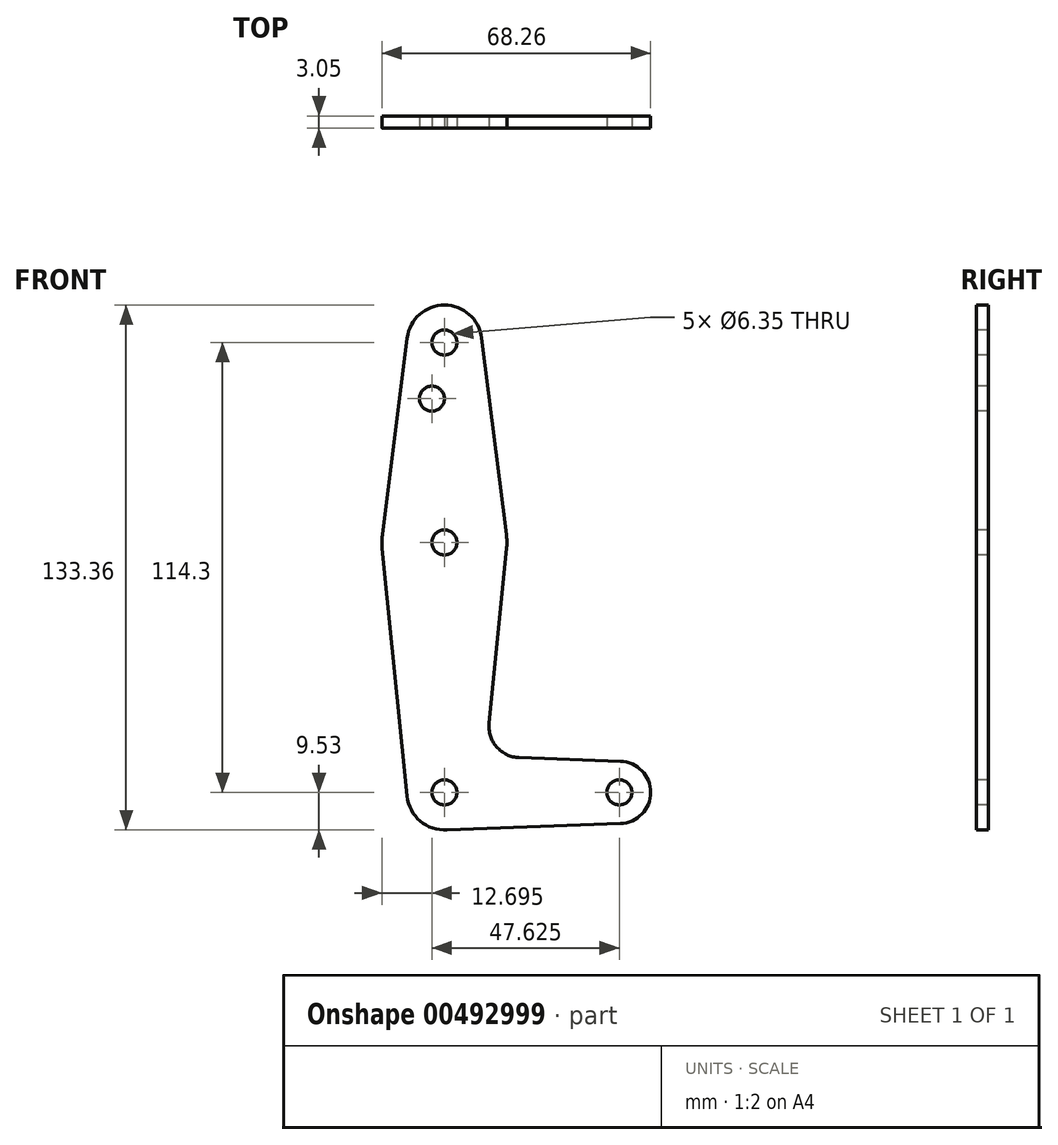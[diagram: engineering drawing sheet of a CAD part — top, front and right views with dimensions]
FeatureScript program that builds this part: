
annotation { "Feature Type Name" : "Feature", "Feature Type Description" : "" }
export const myFeature = defineFeature(function(context is Context, id is Id, definition is map)
    precondition{}
    {
        {
            var Q0;
            Q0=qCreatedBy(makeId("Front.planeOp"),FACE);
            var sketch = newSketch(context, id + "F0", { "sketchPlane" : qUnion([Q0])});
            skCircle(sketch, "E0", {"center": v(0, 0) * mm, "radius": 9.53 * mm});
            skCircle(sketch, "E1", {"center": v(0, 63.5) * mm, "radius": 15.88 * mm});
            skCircle(sketch, "E2", {"center": v(0, 114.3) * mm, "radius": 9.52 * mm});
            skCircle(sketch, "E3", {"center": v(44.45, 0) * mm, "radius": 7.94 * mm});
            skLineSegment(sketch, "E4", {"start": v(0, 0) * mm, "end": v(44.45, 0) * mm, "construction": true});
            skLineSegment(sketch, "E5", {"start": v(0, 114.3) * mm, "end": v(0, 0) * mm, "construction": true});
            skLineSegment(sketch, "E6", {"start": v(-9.45, 115.5) * mm, "end": v(-15.75, 65.48) * mm});
            skLineSegment(sketch, "E7", {"start": v(9.45, 115.5) * mm, "end": v(15.75, 65.48) * mm});
            skLineSegment(sketch, "E8", {"start": v(0, -9.53) * mm, "end": v(44.73, -7.93) * mm});
            skLineSegment(sketch, "E9", {"start": v(18.97, 8.85) * mm, "end": v(44.73, 7.93) * mm});
            skCircle(sketch, "E10", {"center": v(0, 114.3) * mm, "radius": 3.18 * mm});
            skCircle(sketch, "E11", {"center": v(0, 63.5) * mm, "radius": 3.18 * mm});
            skCircle(sketch, "E12", {"center": v(0, 0) * mm, "radius": 3.18 * mm});
            skCircle(sketch, "E13", {"center": v(44.45, 0) * mm, "radius": 3.18 * mm});
            skCircle(sketch, "E14", {"center": v(-3.18, 100.03) * mm, "radius": 3.18 * mm});
            skLineSegment(sketch, "E15", {"start": v(-15.8, 61.91) * mm, "end": v(-9.48, -0.95) * mm});
            skLineSegment(sketch, "E16", {"start": v(15.8, 61.91) * mm, "end": v(11.34, 17.59) * mm});
            skPoint(sketch, "E17.newPointA", {"position": v(9.48, -0.95) * mm});
            skArc(sketch, "E17.filletArc", {"start": v(11.34, 17.59) * mm, "mid": v(13.26, 11.57) * mm, "end": v(18.97, 8.85) * mm});
            skSolve(sketch);
        }
        {
            var Q0;
            Q0 = qSketchRegion(id + "F0", true);
            extrude(context, id + "F1", {"entities" : qUnion([Q0]), "oppositeDirection" : true, "depth" : 3.05 * mm});
        }
    });
